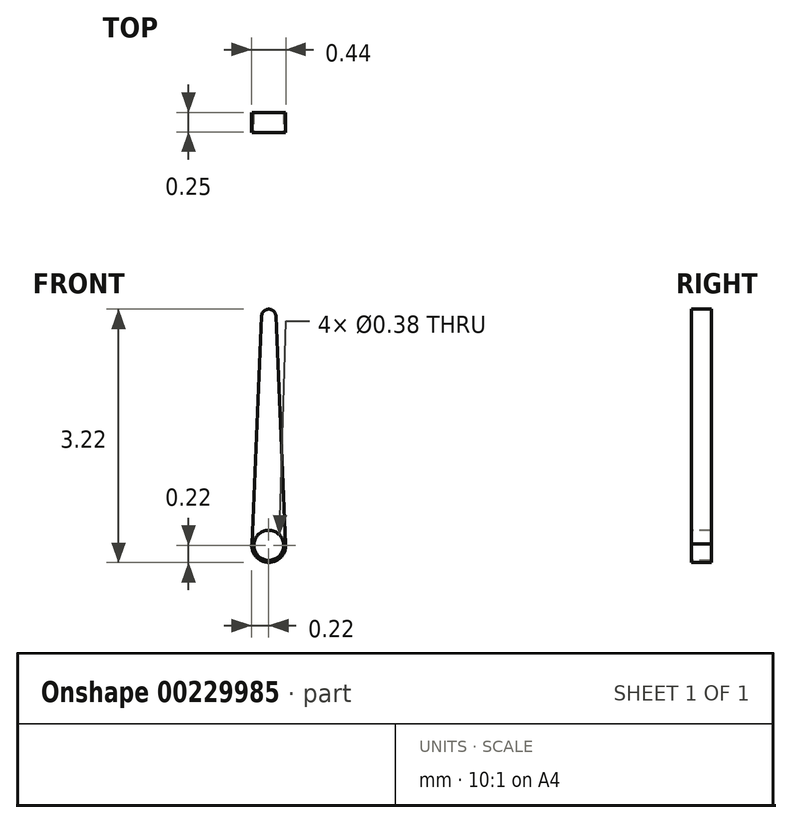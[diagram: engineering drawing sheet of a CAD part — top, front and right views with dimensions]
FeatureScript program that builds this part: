
annotation { "Feature Type Name" : "Feature", "Feature Type Description" : "" }
export const myFeature = defineFeature(function(context is Context, id is Id, definition is map)
    precondition{}
    {
        {
            var Q0;
            Q0=qCreatedBy(makeId("Front.planeOp"),FACE);
            var sketch = newSketch(context, id + "F0", { "sketchPlane" : qUnion([Q0])});
            skArc(sketch, "E0", {"start": v(-0.21, 0.03) * mm, "mid": v(0, -0.22) * mm, "end": v(0.21, 0.03) * mm});
            skLineSegment(sketch, "E1", {"start": v(-0.22, 0) * mm, "end": v(-0.21, 0.03) * mm});
            skLineSegment(sketch, "E2", {"start": v(0, 3) * mm, "end": v(0, 0) * mm, "construction": true});
            skLineSegment(sketch, "E3.0.MirrorCS", {"start": v(0.22, 0) * mm, "end": v(0.21, 0.03) * mm});
            skLineSegment(sketch, "E4", {"start": v(-0.22, 0) * mm, "end": v(-0.1, 2.91) * mm});
            skLineSegment(sketch, "E5", {"start": v(0, 3) * mm, "end": v(0, 3) * mm});
            skPoint(sketch, "E6.visualSharp", {"position": v(-0.09, 3) * mm});
            skArc(sketch, "E6.filletArc", {"start": v(0, 3) * mm, "mid": v(-0.06, 2.97) * mm, "end": v(-0.1, 2.91) * mm});
            skLineSegment(sketch, "E7.0.MirrorCS", {"start": v(0.22, 0) * mm, "end": v(0.1, 2.91) * mm});
            skArc(sketch, "E8.0.MirrorCS", {"start": v(0, 3) * mm, "mid": v(0.06, 2.97) * mm, "end": v(0.1, 2.91) * mm});
            skSolve(sketch);
        }
        {
            var Q0;
            Q0=qSketchRegion(id+"F0",true);
            extrude(context, id + "F1", {"entities" : qUnion([Q0]), "depth" : 0.25 * mm});
        }
        {
            var Q0;
            Q0=makeQuery(id+"F1.opExtrude","CAP_FACE",FACE,{"disambiguationData":[OSD([sQuery(id+"F0.wireOp",EDGE,"E0"),sQuery(id+"F0.wireOp",EDGE,"E4"),sQuery(id+"F0.wireOp",EDGE,"E7.0.MirrorCS"),sQuery(id+"F0.wireOp",EDGE,"E8.0.MirrorCS")])],"isStart":false});
            var sketch = newSketch(context, id + "F2", { "sketchPlane" : qUnion([Q0])});
            skCircle(sketch, "E9", {"center": v(0, 0) * mm, "radius": 0.2 * mm});
            skSolve(sketch);
        }
        {
            var Q0;
            Q0=makeQuery(id+"F2.imprint","IMPRINT",FACE,{"disambiguationData":[TD([[makeQuery(id+"F2.imprint","IMPRINT",EDGE,{"derivedFrom":sQuery(id+"F2.wireOp",EDGE,"E9")}),1.0]])]});
            extrude(context, id + "F3", {"entities" : qUnion([Q0]), "operationType" : NewBodyOperationType.REMOVE, "endBound" : BoundingType.THROUGH_ALL, "oppositeDirection" : true, "depth" : 25.4 * mm});
        }
    });
